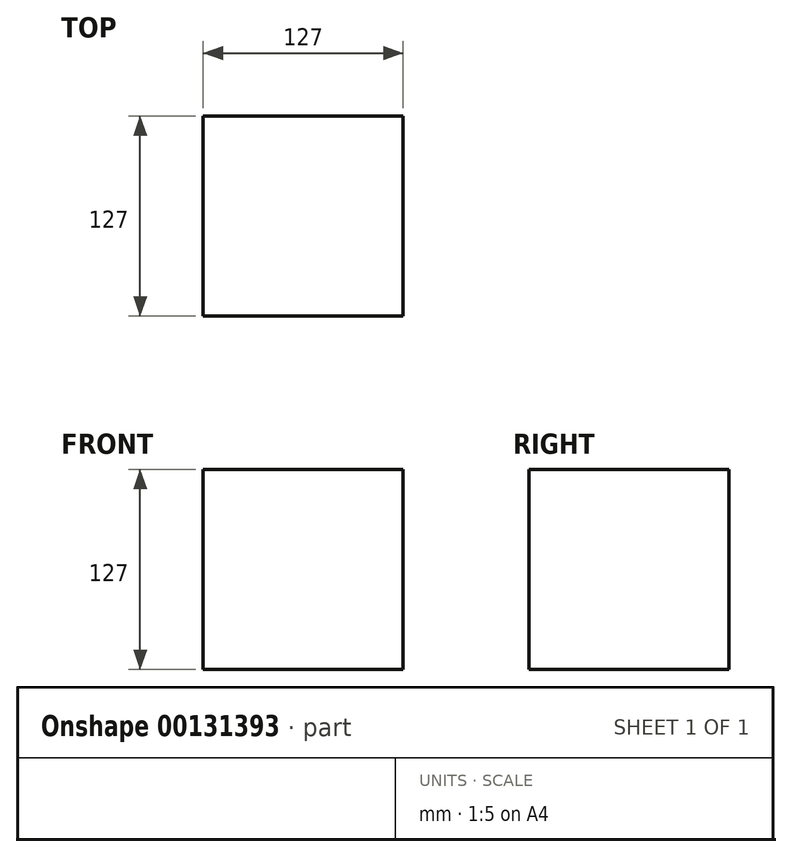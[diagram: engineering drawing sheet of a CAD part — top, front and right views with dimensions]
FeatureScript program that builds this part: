
annotation { "Feature Type Name" : "Feature", "Feature Type Description" : "" }
export const myFeature = defineFeature(function(context is Context, id is Id, definition is map)
    precondition{}
    {
        {
            var Q0;
            Q0=qCreatedBy(makeId("Front.planeOp"),FACE);
            var sketch = newSketch(context, id + "F0", { "sketchPlane" : qUnion([Q0])});
            skLineSegment(sketch, "E0.bottom", {"start": v(63.5, -63.5) * mm, "end": v(-63.5, -63.5) * mm});
            skLineSegment(sketch, "E0.top", {"start": v(63.5, 63.5) * mm, "end": v(-63.5, 63.5) * mm});
            skLineSegment(sketch, "E0.left", {"start": v(63.5, -63.5) * mm, "end": v(63.5, 63.5) * mm});
            skLineSegment(sketch, "E0.right", {"start": v(-63.5, -63.5) * mm, "end": v(-63.5, 63.5) * mm});
            skPoint(sketch, "E0.middle", {"position": v(0, 0) * mm});
            skSolve(sketch);
        }
        {
            var Q0;
            Q0 = qSketchRegion(id + "F0", true);
            extrude(context, id + "F1", {"entities" : qUnion([Q0]), "endBound" : BoundingType.SYMMETRIC, "depth" : 127 * mm});
        }
    });
